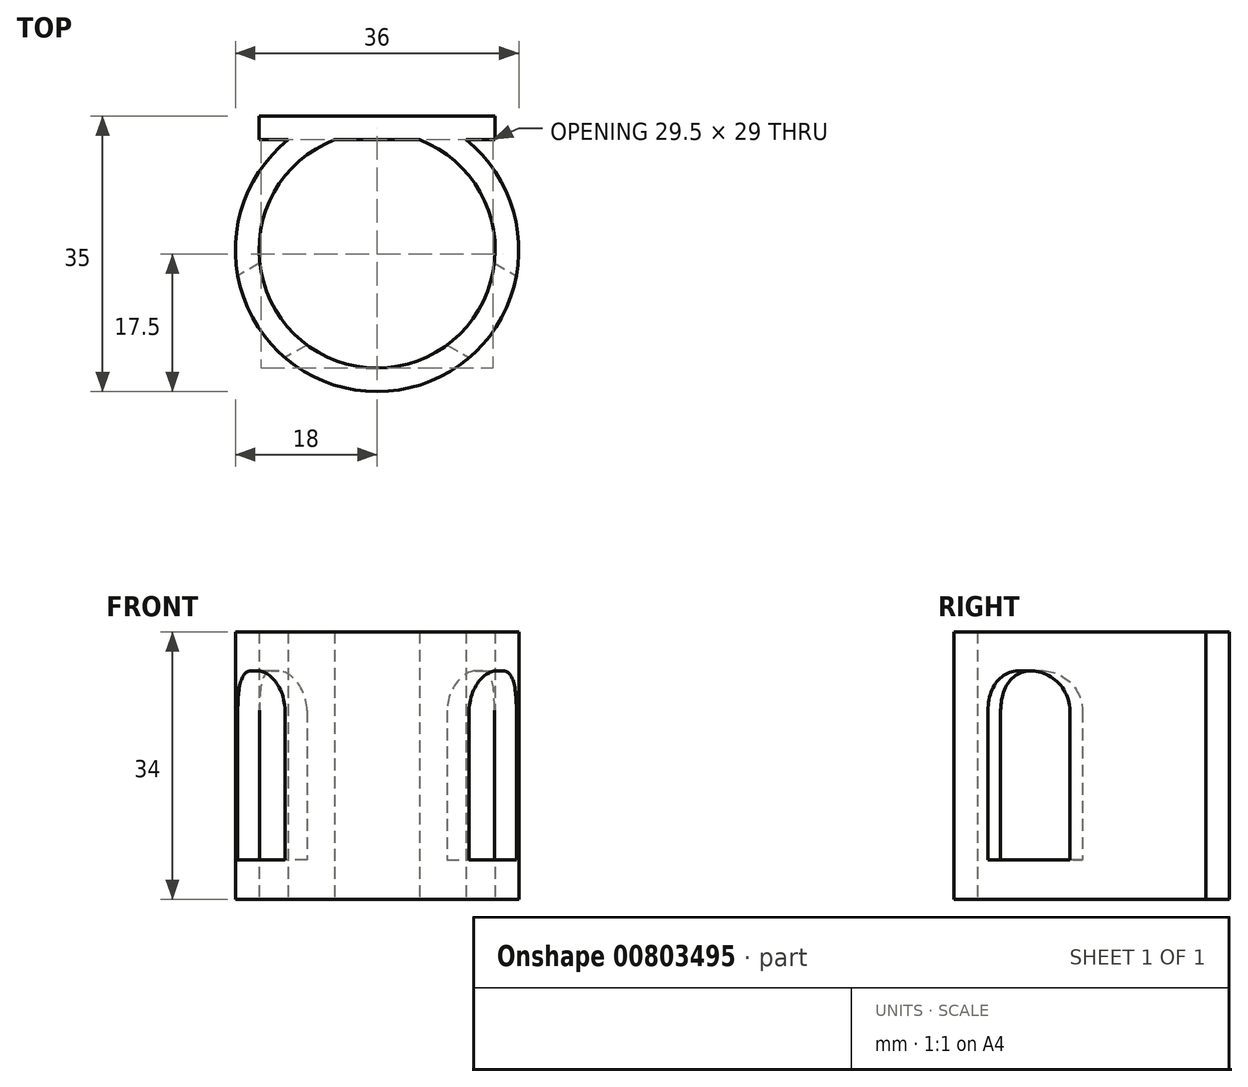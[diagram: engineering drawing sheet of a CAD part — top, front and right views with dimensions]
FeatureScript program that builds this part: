
annotation { "Feature Type Name" : "Feature", "Feature Type Description" : "" }
export const myFeature = defineFeature(function(context is Context, id is Id, definition is map)
    precondition{}
    {
        {
            var Q0;
            Q0=qCreatedBy(makeId("Top.planeOp"),FACE);
            var sketch = newSketch(context, id + "F0", { "sketchPlane" : qUnion([Q0])});
            skArc(sketch, "E0", {"start": v(-5.39, 14) * mm, "mid": v(0, -15) * mm, "end": v(5.39, 14) * mm});
            skArc(sketch, "E1", {"start": v(-11.31, 14) * mm, "mid": v(0, -18) * mm, "end": v(11.31, 14) * mm});
            skLineSegment(sketch, "E2.bottom", {"start": v(-15, 17) * mm, "end": v(15, 17) * mm});
            skLineSegment(sketch, "E2.top", {"start": v(-15, 14) * mm, "end": v(-11.31, 14) * mm});
            skLineSegment(sketch, "E2.left", {"start": v(-15, 17) * mm, "end": v(-15, 14) * mm});
            skLineSegment(sketch, "E2.right", {"start": v(15, 17) * mm, "end": v(15, 14) * mm});
            skLineSegment(sketch, "E3.trimOffspring", {"start": v(11.31, 14) * mm, "end": v(15, 14) * mm});
            skLineSegment(sketch, "E4.trimOffspring", {"start": v(-5.39, 14) * mm, "end": v(5.39, 14) * mm});
            skPoint(sketch, "E5", {"position": v(0, 17) * mm});
            skLineSegment(sketch, "E6", {"start": v(0, 0) * mm, "end": v(-33.62, -19.41) * mm, "construction": true});
            skLineSegment(sketch, "E7", {"start": v(0, 0) * mm, "end": v(0, 35.5) * mm, "construction": true});
            skLineSegment(sketch, "E8", {"start": v(0, 0) * mm, "end": v(27.46, -15.85) * mm, "construction": true});
            skPoint(sketch, "E9", {"position": v(-15.59, -9) * mm});
            skPoint(sketch, "E10", {"position": v(15.59, -9) * mm});
            skSolve(sketch);
        }
        {
            var Q0;
            Q0 = qSketchRegion(id + "F0", true);
            extrude(context, id + "F1", {"entities" : qUnion([Q0]), "depth" : 34 * mm, "offsetDistance" : 25 * mm});
        }
        {
            var Q0;
            Q0=qCreatedBy(makeId("Front.planeOp"),FACE);
            var sketch = newSketch(context, id + "F2", { "sketchPlane" : qUnion([Q0])});
            skLineSegment(sketch, "E11", {"start": v(0, 56.52) * mm, "end": v(0, -58.25) * mm, "construction": true});
            skLineSegment(sketch, "E12.0", {"start": v(15, 34) * mm, "end": v(15, 0) * mm});
            skLineSegment(sketch, "E13.0", {"start": v(-15, 34) * mm, "end": v(-15, 0) * mm});
            skLineSegment(sketch, "E14.0", {"start": v(-15, 34) * mm, "end": v(15, 34) * mm});
            skLineSegment(sketch, "E15.0", {"start": v(-15, 0) * mm, "end": v(15, 0) * mm});
            skPoint(sketch, "E16", {"position": v(0, 17) * mm});
            skPoint(sketch, "E16.positionSnap0", {"position": v(15, 17) * mm});
            skCircle(sketch, "E17", {"center": v(0, 17) * mm, "radius": 15 * mm});
            skSolve(sketch);
        }
        {
            var Q0;
            Q0=sQuery(id+"F0.wireOp",VERTEX,"E9");
            var Q1;
            Q1=sQuery(id+"F0.wireOp",EDGE,"E1");
            cPlane(context, id + "F3", {"entities" : qUnion([Q0, Q1]), "cplaneType" : CPlaneType.CURVE_POINT, "offset" : 25 * mm, "width" : 150 * mm, "height" : 150 * mm});
        }
        {
            var Q0;
            Q0=sQuery(id+"F0.wireOp",VERTEX,"E10");
            var Q1;
            Q1=sQuery(id+"F0.wireOp",EDGE,"E1");
            cPlane(context, id + "F4", {"entities" : qUnion([Q0, Q1]), "cplaneType" : CPlaneType.CURVE_POINT, "offset" : 25 * mm, "width" : 150 * mm, "height" : 150 * mm});
        }
        {
            var Q0;
            Q0=qCreatedBy(id+"F3.planeOp",FACE);
            var sketch = newSketch(context, id + "F5", { "sketchPlane" : qUnion([Q0])});
            skPoint(sketch, "E18.0", {"position": v(-18, 0) * mm});
            skLineSegment(sketch, "E19", {"start": v(-18, 0) * mm, "end": v(-18, 70.07) * mm, "construction": true});
            skSolve(sketch);
        }
        {
            var Q0;
            Q0=sQuery(id+"F5.wireOp",EDGE,"E19");
            var Q1;
            Q1=qCreatedBy(id+"F3.planeOp",FACE);
            cPlane(context, id + "F6", {"entities" : qUnion([Q0, Q1]), "cplaneType" : CPlaneType.LINE_ANGLE, "offset" : 25 * mm, "angle" : 90 * degree, "width" : 150 * mm, "height" : 150 * mm});
        }
        {
            var Q0;
            Q0=qCreatedBy(id+"F4.planeOp",FACE);
            var sketch = newSketch(context, id + "F7", { "sketchPlane" : qUnion([Q0])});
            skPoint(sketch, "E20.0", {"position": v(-18, 0) * mm});
            skLineSegment(sketch, "E21", {"start": v(-18, 0) * mm, "end": v(-18, 71.65) * mm, "construction": true});
            skSolve(sketch);
        }
        {
            var Q0;
            Q0=qCreatedBy(id+"F4.planeOp",FACE);
            var Q1;
            Q1=sQuery(id+"F7.wireOp",EDGE,"E21");
            cPlane(context, id + "F8", {"entities" : qUnion([Q0, Q1]), "cplaneType" : CPlaneType.LINE_ANGLE, "offset" : 25 * mm, "angle" : 90 * degree, "width" : 150 * mm, "height" : 150 * mm});
        }
        {
            var Q0;
            Q0=qCreatedBy(id+"F6.planeOp",FACE);
            var sketch = newSketch(context, id + "F9", { "sketchPlane" : qUnion([Q0])});
            skLineSegment(sketch, "E22.0", {"start": v(0, 0) * mm, "end": v(0, 70.07) * mm});
            skLineSegment(sketch, "E23", {"start": v(0, 29) * mm, "end": v(-6, 29) * mm});
            skLineSegment(sketch, "E24", {"start": v(-6, 29) * mm, "end": v(-6, 5) * mm});
            skLineSegment(sketch, "E25", {"start": v(-6, 5) * mm, "end": v(0, 5) * mm});
            skLineSegment(sketch, "E26.MirrorCS", {"start": v(0, 29) * mm, "end": v(6, 29) * mm});
            skLineSegment(sketch, "E27.MirrorCS", {"start": v(6, 29) * mm, "end": v(6, 5) * mm});
            skLineSegment(sketch, "E28.MirrorCS", {"start": v(6, 5) * mm, "end": v(0, 5) * mm});
            skSolve(sketch);
        }
        {
            var Q0;
            Q0 = qSketchRegion(id + "F9", true);
            extrude(context, id + "F10", {"entities" : qUnion([Q0]), "operationType" : NewBodyOperationType.REMOVE, "oppositeDirection" : true, "depth" : 10 * mm, "offsetDistance" : 25 * mm});
        }
        {
            var Q0;
            Q0=qCreatedBy(id+"F8.planeOp",FACE);
            var sketch = newSketch(context, id + "F11", { "sketchPlane" : qUnion([Q0])});
            skLineSegment(sketch, "E29.0", {"start": v(0, 0) * mm, "end": v(0, 71.65) * mm});
            skLineSegment(sketch, "E30", {"start": v(0, 29) * mm, "end": v(6, 29) * mm});
            skLineSegment(sketch, "E31", {"start": v(6, 29) * mm, "end": v(6, 5) * mm});
            skLineSegment(sketch, "E32", {"start": v(6, 5) * mm, "end": v(0, 5) * mm});
            skLineSegment(sketch, "E33.MirrorCS", {"start": v(0, 29) * mm, "end": v(-6, 29) * mm});
            skLineSegment(sketch, "E34.MirrorCS", {"start": v(-6, 29) * mm, "end": v(-6, 5) * mm});
            skLineSegment(sketch, "E35.MirrorCS", {"start": v(-6, 5) * mm, "end": v(0, 5) * mm});
            skSolve(sketch);
        }
        {
            var Q0;
            Q0 = qSketchRegion(id + "F11", true);
            extrude(context, id + "F12", {"entities" : qUnion([Q0]), "operationType" : NewBodyOperationType.REMOVE, "oppositeDirection" : true, "depth" : 10 * mm, "offsetDistance" : 25 * mm});
        }
        {
            var Q0;
            Q0=makeQuery(id+"F12.boolean.opBoolean","COPY",EDGE,{"derivedFrom":makeQuery(id+"F12.opExtrude","SWEPT_EDGE",EDGE,{"disambiguationData":[OSD([sQuery(id+"F11.wireOp",EDGE,"E30"),sQuery(id+"F11.wireOp",EDGE,"E31")])]})});
            var Q1;
            Q1=makeQuery(id+"F12.boolean.opBoolean","COPY",EDGE,{"derivedFrom":makeQuery(id+"F12.opExtrude","SWEPT_EDGE",EDGE,{"disambiguationData":[OSD([sQuery(id+"F11.wireOp",EDGE,"E33.MirrorCS"),sQuery(id+"F11.wireOp",EDGE,"E34.MirrorCS")])]})});
            var Q2;
            Q2=makeQuery(id+"F10.boolean.opBoolean","COPY",EDGE,{"derivedFrom":makeQuery(id+"F10.opExtrude","SWEPT_EDGE",EDGE,{"disambiguationData":[OSD([sQuery(id+"F9.wireOp",EDGE,"E23"),sQuery(id+"F9.wireOp",EDGE,"E24")])]})});
            var Q3;
            Q3=makeQuery(id+"F10.boolean.opBoolean","COPY",EDGE,{"derivedFrom":makeQuery(id+"F10.opExtrude","SWEPT_EDGE",EDGE,{"disambiguationData":[OSD([sQuery(id+"F9.wireOp",EDGE,"E26.MirrorCS"),sQuery(id+"F9.wireOp",EDGE,"E27.MirrorCS")])]})});
            fillet(context, id + "F13", {"entities" : qUnion([Q0, Q1, Q2, Q3]), "tangentPropagation" : true, "radius" : 5 * mm, "defaultsChanged" : false, "vertexSettings" : [], "allowEdgeOverflow" : false});
        }
    });
